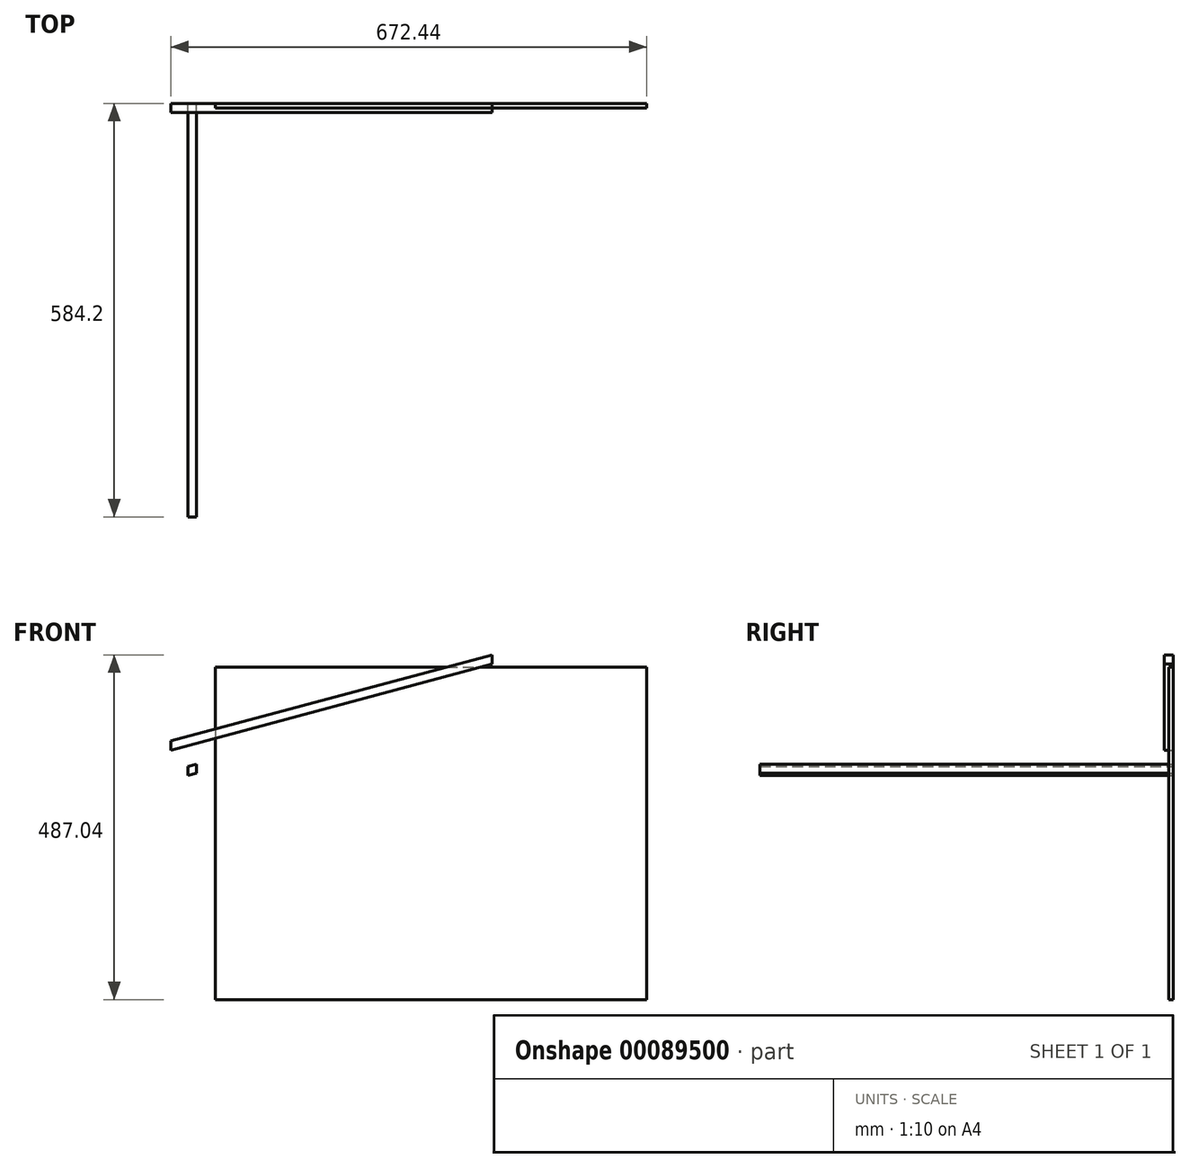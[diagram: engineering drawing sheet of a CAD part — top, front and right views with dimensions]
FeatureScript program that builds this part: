
annotation { "Feature Type Name" : "Feature", "Feature Type Description" : "" }
export const myFeature = defineFeature(function(context is Context, id is Id, definition is map)
    precondition{}
    {
        {
            var Q0;
            Q0=qCreatedBy(makeId("Front.planeOp"),FACE);
            var sketch = newSketch(context, id + "F0", { "sketchPlane" : qUnion([Q0])});
            skLineSegment(sketch, "E0.bottom", {"start": v(-92.74, 30.2) * mm, "end": v(361.15, 151.83) * mm});
            skLineSegment(sketch, "E0.top", {"start": v(-92.74, 17.06) * mm, "end": v(361.15, 138.68) * mm});
            skLineSegment(sketch, "E0.left", {"start": v(-92.74, 30.2) * mm, "end": v(-92.74, 17.06) * mm});
            skLineSegment(sketch, "E0.right", {"start": v(361.15, 151.83) * mm, "end": v(361.15, 138.68) * mm});
            skSolve(sketch);
        }
        {
            var Q0;
            Q0 = qSketchRegion(id + "F0", true);
            extrude(context, id + "F1", {"entities" : qUnion([Q0]), "depth" : 12.7 * mm});
        }
        {
            var Q0;
            Q0=qCreatedBy(makeId("Front.planeOp"),FACE);
            var sketch = newSketch(context, id + "F2", { "sketchPlane" : qUnion([Q0])});
            skLineSegment(sketch, "E1.bottom", {"start": v(-68.76, -6.16) * mm, "end": v(-56.5, -2.87) * mm});
            skLineSegment(sketch, "E1.top", {"start": v(-68.76, -18.86) * mm, "end": v(-56.5, -15.57) * mm});
            skLineSegment(sketch, "E1.left", {"start": v(-68.76, -6.16) * mm, "end": v(-68.76, -18.86) * mm});
            skLineSegment(sketch, "E1.right", {"start": v(-56.5, -2.87) * mm, "end": v(-56.5, -15.57) * mm});
            skSolve(sketch);
        }
        {
            var Q0;
            Q0 = qSketchRegion(id + "F2", true);
            extrude(context, id + "F3", {"entities" : qUnion([Q0]), "depth" : 584.2 * mm});
        }
        {
            var Q0;
            Q0=qCreatedBy(makeId("Front.planeOp"),FACE);
            var sketch = newSketch(context, id + "F4", { "sketchPlane" : qUnion([Q0])});
            skLineSegment(sketch, "E2.bottom", {"start": v(-29.9, 134.7) * mm, "end": v(579.7, 134.7) * mm});
            skLineSegment(sketch, "E2.top", {"start": v(-29.9, -335.2) * mm, "end": v(579.7, -335.2) * mm});
            skLineSegment(sketch, "E2.left", {"start": v(-29.9, 134.7) * mm, "end": v(-29.9, -335.2) * mm});
            skLineSegment(sketch, "E2.right", {"start": v(579.7, 134.7) * mm, "end": v(579.7, -335.2) * mm});
            skSolve(sketch);
        }
        {
            var Q0;
            Q0=makeQuery(id+"F4.imprint","IMPRINT",FACE,{"disambiguationData":[TD([[makeQuery(id+"F4.imprint","IMPRINT",EDGE,{"derivedFrom":sQuery(id+"F4.wireOp",EDGE,"E2.bottom")}),-1.0]])]});
            extrude(context, id + "F5", {"entities" : qUnion([Q0]), "depth" : 6.35 * mm});
        }
    });
